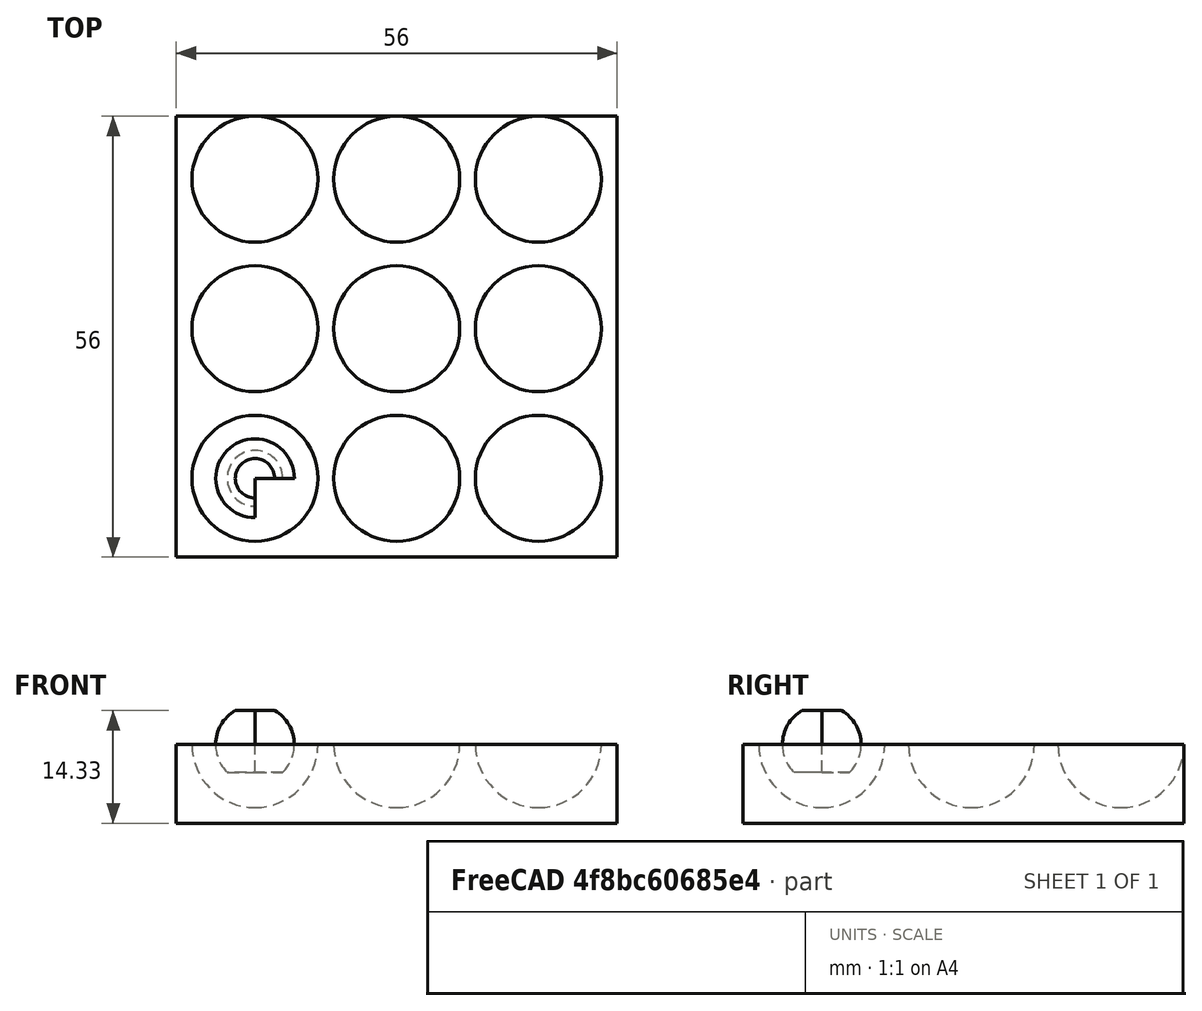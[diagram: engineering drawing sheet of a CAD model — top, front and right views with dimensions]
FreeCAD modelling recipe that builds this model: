
FCSTD DOCUMENT  (FreeCAD 0.18R16146 (Git))
Label: esferas_dani
License: All rights reserved
LicenseURL: http://en.wikipedia.org/wiki/All_rights_reserved
objects: Part::Sphere×2, Part::FeaturePython×1, Part::Box×1, Part::Cut×1
note: 5 computed .brp shape members not serialized (recipe doc carries the construction recipe); baked Part::Feature solids carry a one-line shape summary decoded from their .brp

FEATURE [Part::Sphere] Sphere  label="pac-man"
  Angle1 = -45
  Angle2 = 60
  Angle3 = 270
  AttacherType = Attacher::AttachEngine3D
  Radius = 5
FEATURE [Part::Sphere] Sphere001  label="Esfera"
  Angle1 = -90
  Angle2 = 90
  Angle3 = 360
  AttacherType = Attacher::AttachEngine3D
  Radius = 8
FEATURE [Part::FeaturePython] Array  # Draft array (typed FeaturePython)
  Angle = 360
  ArrayType = 0
  Axis = (0,0,1)
  Base = -> Sphere001
  Center = (0,0,0)
  Fuse = false
  IntervalAxis = (0,0,0)
  IntervalX = (18,0,0)
  IntervalY = (0,19,0)
  IntervalZ = (0,0,1)
  NumberPolar = 1
  NumberX = 3
  NumberY = 3
  NumberZ = 1
FEATURE [Part::Box] Box  label="Cubo"
  AttacherType = Attacher::AttachEngine3D
  Height = 10
  Length = 56
  Placement = pos=(-10,-10,-10) rot=(0,0,1;0rad)
  Width = 56
FEATURE [Part::Cut] Cut
  Base = -> Box
  Refine = true
  Tool = -> Array
